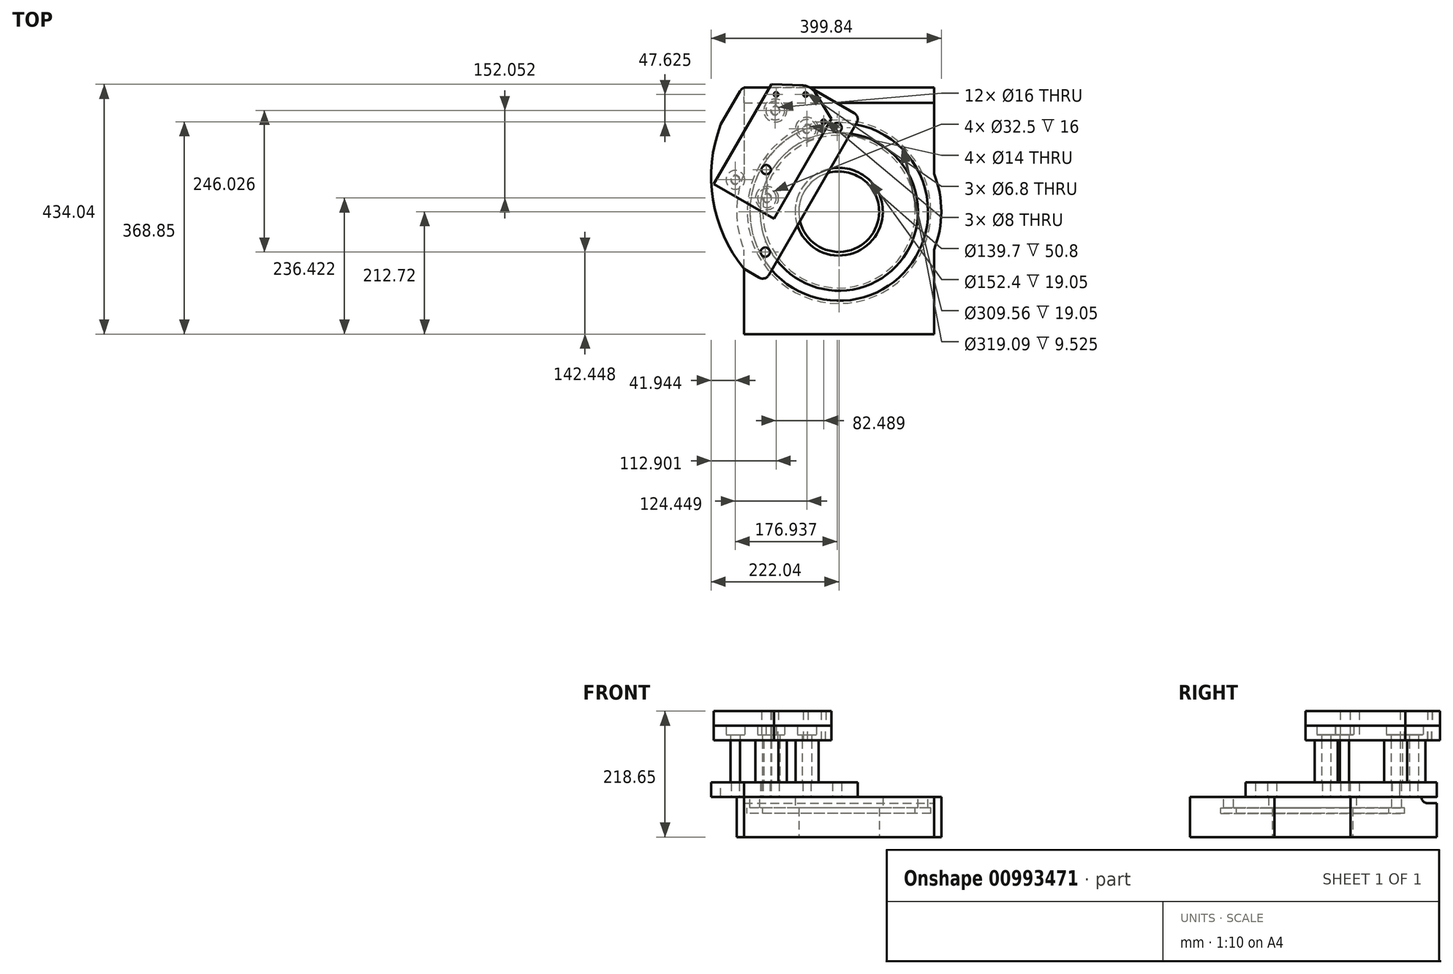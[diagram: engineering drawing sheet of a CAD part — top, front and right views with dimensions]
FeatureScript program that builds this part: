
annotation { "Feature Type Name" : "Feature", "Feature Type Description" : "" }
export const myFeature = defineFeature(function(context is Context, id is Id, definition is map)
    precondition{}
    {
        {
            var Q0;
            Q0=qCreatedBy(makeId("Top.planeOp"),FACE);
            var sketch = newSketch(context, id + "F0", { "sketchPlane" : qUnion([Q0])});
            skCircle(sketch, "E0", {"center": v(0, 0) * mm, "radius": 69.85 * mm});
            skCircle(sketch, "E1", {"center": v(0, 0) * mm, "radius": 76.2 * mm});
            skCircle(sketch, "E2", {"center": v(0, 0) * mm, "radius": 162.72 * mm});
            skCircle(sketch, "E3", {"center": v(0, 0) * mm, "radius": 137.32 * mm});
            skCircle(sketch, "E4", {"center": v(0, 0) * mm, "radius": 177.8 * mm});
            skLineSegment(sketch, "E5", {"start": v(0, 0) * mm, "end": v(0, 215.9) * mm, "construction": true});
            skLineSegment(sketch, "E6", {"start": v(0, 0) * mm, "end": v(0, -212.73) * mm, "construction": true});
            skLineSegment(sketch, "E7", {"start": v(0, 215.9) * mm, "end": v(-165.1, 215.9) * mm});
            skLineSegment(sketch, "E8", {"start": v(0, 215.9) * mm, "end": v(165.1, 215.9) * mm});
            skLineSegment(sketch, "E9", {"start": v(165.1, 215.9) * mm, "end": v(165.1, 66) * mm});
            skLineSegment(sketch, "E10", {"start": v(-165.1, 215.9) * mm, "end": v(-165.1, 66) * mm});
            skLineSegment(sketch, "E11", {"start": v(0, -212.72) * mm, "end": v(165.1, -212.72) * mm});
            skLineSegment(sketch, "E12", {"start": v(0, -212.73) * mm, "end": v(-165.1, -212.73) * mm});
            skLineSegment(sketch, "E13", {"start": v(165.1, -212.72) * mm, "end": v(165.1, -66) * mm});
            skLineSegment(sketch, "E14", {"start": v(-165.1, -212.73) * mm, "end": v(-165.1, -66) * mm});
            skSolve(sketch);
        }
        {
            var Q0;
            Q0=makeQuery(id+"F0.imprint","IMPRINT",FACE,{"disambiguationData":[TD([[makeQuery(id+"F0.imprint","IMPRINT",EDGE,{"derivedFrom":sQuery(id+"F0.wireOp",EDGE,"E11")}),1.0]])]});
            var Q1;
            Q1=makeQuery(id+"F0.imprint","IMPRINT",FACE,{"disambiguationData":[TD([[makeQuery(id+"F0.imprint","IMPRINT",EDGE,{"derivedFrom":sQuery(id+"F0.wireOp",EDGE,"E7")}),1.0]])]});
            var Q2;
            Q2=makeQuery(id+"F0.imprint","IMPRINT",FACE,{"disambiguationData":[TD([[makeQuery(id+"F0.imprint","IMPRINT",EDGE,{"derivedFrom":sQuery(id+"F0.wireOp",EDGE,"E2")}),-1.0]])]});
            var Q3;
            Q3=makeQuery(id+"F0.imprint","IMPRINT",FACE,{"disambiguationData":[TD([[makeQuery(id+"F0.imprint","IMPRINT",EDGE,{"derivedFrom":sQuery(id+"F0.wireOp",EDGE,"E2")}),1.0]])]});
            var Q4;
            Q4=makeQuery(id+"F0.imprint","IMPRINT",FACE,{"disambiguationData":[TD([[makeQuery(id+"F0.imprint","IMPRINT",EDGE,{"derivedFrom":sQuery(id+"F0.wireOp",EDGE,"E1")}),-1.0]])]});
            var Q5;
            Q5=makeQuery(id+"F0.imprint","IMPRINT",FACE,{"disambiguationData":[TD([[makeQuery(id+"F0.imprint","IMPRINT",EDGE,{"derivedFrom":sQuery(id+"F0.wireOp",EDGE,"E0")}),-1.0]])]});
            extrude(context, id + "F1", {"entities" : qUnion([Q0, Q1, Q2, Q3, Q4, Q5]), "depth" : 69.85 * mm, "offsetDistance" : 25.4 * mm});
        }
        {
            var Q0;
            Q0=makeQuery(id+"F0.imprint","IMPRINT",FACE,{"disambiguationData":[TD([[makeQuery(id+"F0.imprint","IMPRINT",EDGE,{"derivedFrom":sQuery(id+"F0.wireOp",EDGE,"E0")}),-1.0]])]});
            var Q1;
            Q1=makeQuery(id+"F1.opExtrude","CAP_FACE",FACE,{"disambiguationData":[OSD([sQuery(id+"F0.wireOp",EDGE,"E0"),sQuery(id+"F0.wireOp",EDGE,"E4"),sQuery(id+"F0.wireOp",EDGE,"E7"),sQuery(id+"F0.wireOp",EDGE,"E8"),sQuery(id+"F0.wireOp",EDGE,"E9"),sQuery(id+"F0.wireOp",EDGE,"E10"),sQuery(id+"F0.wireOp",EDGE,"E11"),sQuery(id+"F0.wireOp",EDGE,"E12"),sQuery(id+"F0.wireOp",EDGE,"E13"),sQuery(id+"F0.wireOp",EDGE,"E14")])],"isStart":false});
            var Q2;
            Q2=makeQuery(id+"F1.opExtrude","CAP_FACE",FACE,{"disambiguationData":[OSD([sQuery(id+"F0.wireOp",EDGE,"E0"),sQuery(id+"F0.wireOp",EDGE,"E4"),sQuery(id+"F0.wireOp",EDGE,"E7"),sQuery(id+"F0.wireOp",EDGE,"E8"),sQuery(id+"F0.wireOp",EDGE,"E9"),sQuery(id+"F0.wireOp",EDGE,"E10"),sQuery(id+"F0.wireOp",EDGE,"E11"),sQuery(id+"F0.wireOp",EDGE,"E12"),sQuery(id+"F0.wireOp",EDGE,"E13"),sQuery(id+"F0.wireOp",EDGE,"E14")])],"isStart":false});
            extrude(context, id + "F2", {"entities" : qUnion([Q0]), "operationType" : NewBodyOperationType.REMOVE, "endBound" : BoundingType.UP_TO_SURFACE, "depth" : 19.05 * mm, "endBoundEntityFace" : qUnion([Q1]), "offsetDistance" : 25.4 * mm, "hasSecondDirection" : true, "secondDirectionBound" : BoundingType.UP_TO_SURFACE, "secondDirectionOppositeDirection" : false, "secondDirectionDepth" : 25.4 * mm, "secondDirectionBoundEntityFace" : qUnion([Q2]), "hasSecondDirectionOffset" : true, "secondDirectionOffsetDistance" : 19.05 * mm});
        }
        {
            var Q0;
            Q0=qCreatedBy(makeId("Right.planeOp"),FACE);
            var sketch = newSketch(context, id + "F3", { "sketchPlane" : qUnion([Q0])});
            skLineSegment(sketch, "E15.0", {"start": v(215.9, 69.85) * mm, "end": v(66, 69.85) * mm});
            skLineSegment(sketch, "E16.0", {"start": v(66, 69.85) * mm, "end": v(-66, 69.85) * mm});
            skLineSegment(sketch, "E17.0", {"start": v(-212.73, 69.85) * mm, "end": v(-66, 69.85) * mm});
            skLineSegment(sketch, "E18.0", {"start": v(215.9, 69.85) * mm, "end": v(215.9, 0) * mm});
            skLineSegment(sketch, "E19.0", {"start": v(-212.73, 69.85) * mm, "end": v(-212.73, 0) * mm});
            skLineSegment(sketch, "E20.0", {"start": v(-212.73, 0) * mm, "end": v(-66, 0) * mm});
            skLineSegment(sketch, "E21.0", {"start": v(-162.72, 0) * mm, "end": v(162.72, 0) * mm});
            skLineSegment(sketch, "E22.0", {"start": v(215.9, 0) * mm, "end": v(66, 0) * mm});
            skLineSegment(sketch, "E23", {"start": v(215.9, 58.74) * mm, "end": v(188.91, 58.74) * mm});
            skLineSegment(sketch, "E24", {"start": v(188.91, 58.74) * mm, "end": v(188.91, 69.85) * mm, "construction": true});
            skPoint(sketch, "E25", {"position": v(200.02, 69.85) * mm});
            skArc(sketch, "E26", {"start": v(188.91, 69.85) * mm, "mid": v(192.17, 62) * mm, "end": v(200.02, 58.74) * mm});
            skLineSegment(sketch, "E27", {"start": v(0, 0) * mm, "end": v(0, 69.85) * mm, "construction": true});
            skPoint(sketch, "E28", {"position": v(137.32, 69.85) * mm});
            skPoint(sketch, "E29", {"position": v(154.78, 69.85) * mm});
            skLineSegment(sketch, "E30", {"start": v(154.78, 69.85) * mm, "end": v(154.78, 50.8) * mm});
            skLineSegment(sketch, "E31", {"start": v(137.32, 69.85) * mm, "end": v(137.32, 50.8) * mm});
            skLineSegment(sketch, "E32", {"start": v(154.78, 50.8) * mm, "end": v(159.54, 50.8) * mm});
            skLineSegment(sketch, "E33", {"start": v(137.32, 50.8) * mm, "end": v(132.56, 50.8) * mm});
            skLineSegment(sketch, "E34", {"start": v(159.54, 50.8) * mm, "end": v(159.54, 41.28) * mm});
            skLineSegment(sketch, "E35", {"start": v(159.54, 41.28) * mm, "end": v(132.56, 41.28) * mm});
            skLineSegment(sketch, "E36", {"start": v(132.56, 41.28) * mm, "end": v(132.56, 50.8) * mm});
            skSolve(sketch);
        }
        {
            var Q0;
            {var subQ3=sQuery(id+"F3.wireOp",EDGE,"E26");Q0=makeQuery(id+"F3.imprint","IMPRINT",FACE,{"disambiguationData":[TD([[makeQuery(id+"F3.imprint","IMPRINT",EDGE,{"derivedFrom":subQ3}),1.0]])]});}
            extrude(context, id + "F4", {"entities" : qUnion([Q0]), "operationType" : NewBodyOperationType.REMOVE, "endBound" : BoundingType.THROUGH_ALL, "oppositeDirection" : true, "depth" : 25.4 * mm, "offsetDistance" : 25.4 * mm, "hasSecondDirection" : true, "secondDirectionBound" : BoundingType.THROUGH_ALL, "secondDirectionOppositeDirection" : false, "secondDirectionDepth" : 25.4 * mm});
        }
        {
            var Q0;
            {var subQ1=sQuery(id+"F3.wireOp",EDGE,"E30");Q0=makeQuery(id+"F3.imprint","IMPRINT",FACE,{"disambiguationData":[TD([[makeQuery(id+"F3.imprint","IMPRINT",EDGE,{"derivedFrom":subQ1}),-1.0]])]});}
            var Q1;
            Q1=sQuery(id+"F3.wireOp",EDGE,"E27");
            revolve(context, id + "F5", {"operationType" : NewBodyOperationType.REMOVE, "surfaceOperationType" : NewSurfaceOperationType.NEW, "entities" : qUnion([Q0]), "axis" : qUnion([Q1]), "revolveType" : RevolveType.FULL, "oppositeDirection" : true});
        }
        {
            var Q0;
            {var subQ0=sQuery(id+"F0.wireOp",EDGE,"E10");var subQ1=sQuery(id+"F0.wireOp",EDGE,"E9");var subQ2=sQuery(id+"F0.wireOp",EDGE,"E4");var subQ3=sQuery(id+"F0.wireOp",EDGE,"E13");var subQ4=sQuery(id+"F0.wireOp",EDGE,"E14");var subQ5=sQuery(id+"F0.wireOp",EDGE,"E12");var subQ6=sQuery(id+"F0.wireOp",EDGE,"E11");Q0=makeQuery(id+"F5.boolean.opBoolean","SPLIT",FACE,{"disambiguationData":[TD([makeQuery(id+"F1.opExtrude","SWEPT_FACE",FACE,{"disambiguationData":[OSD([subQ1])]})])],"derivedFrom":makeQuery(id+"F1.opExtrude","CAP_FACE",FACE,{"disambiguationData":[OSD([sQuery(id+"F0.wireOp",EDGE,"E0"),subQ2,sQuery(id+"F0.wireOp",EDGE,"E7"),sQuery(id+"F0.wireOp",EDGE,"E8"),subQ1,subQ0,subQ6,subQ5,subQ3,subQ4])],"isStart":false})});}
            cPlane(context, id + "F6", {"entities" : qUnion([Q0]), "cplaneType" : CPlaneType.OFFSET, "offset" : 225 * mm, "width" : 152.4 * mm, "height" : 152.4 * mm});
        }
        {
            var Q0;
            {var subQ0=sQuery(id+"F0.wireOp",EDGE,"E10");var subQ1=sQuery(id+"F0.wireOp",EDGE,"E9");var subQ2=sQuery(id+"F0.wireOp",EDGE,"E4");var subQ3=sQuery(id+"F0.wireOp",EDGE,"E13");var subQ4=sQuery(id+"F0.wireOp",EDGE,"E14");var subQ5=sQuery(id+"F0.wireOp",EDGE,"E12");var subQ6=sQuery(id+"F0.wireOp",EDGE,"E11");Q0=makeQuery(id+"F5.boolean.opBoolean","SPLIT",FACE,{"disambiguationData":[TD([makeQuery(id+"F1.opExtrude","SWEPT_FACE",FACE,{"disambiguationData":[OSD([subQ1])]})])],"derivedFrom":makeQuery(id+"F1.opExtrude","CAP_FACE",FACE,{"disambiguationData":[OSD([sQuery(id+"F0.wireOp",EDGE,"E0"),subQ2,sQuery(id+"F0.wireOp",EDGE,"E7"),sQuery(id+"F0.wireOp",EDGE,"E8"),subQ1,subQ0,subQ6,subQ5,subQ3,subQ4])],"isStart":false})});}
            var sketch = newSketch(context, id + "F7", { "sketchPlane" : qUnion([Q0])});
            skLineSegment(sketch, "E37.0", {"start": v(-165.1, 215.9) * mm, "end": v(165.1, 215.9) * mm});
            skPoint(sketch, "E38", {"position": v(-50.8, 215.9) * mm});
            skLineSegment(sketch, "E39", {"start": v(-50.8, 215.9) * mm, "end": v(-127.79, 260.35) * mm});
            skLineSegment(sketch, "E40", {"start": v(-50.8, 215.9) * mm, "end": v(26.19, 171.45) * mm});
            skLineSegment(sketch, "E41", {"start": v(30.84, 154.1) * mm, "end": v(-121.56, -109.86) * mm});
            skLineSegment(sketch, "E42", {"start": v(-145.14, 255.7) * mm, "end": v(-303.89, -19.26) * mm});
            skLineSegment(sketch, "E43", {"start": v(-138.91, -114.51) * mm, "end": v(-303.89, -19.26) * mm});
            skPoint(sketch, "E44", {"position": v(-253.09, 68.73) * mm});
            skLineSegment(sketch, "E45.0", {"start": v(-165.1, -212.73) * mm, "end": v(-165.1, -66) * mm});
            skPoint(sketch, "E46", {"position": v(-165.1, -99.4) * mm});
            skCircle(sketch, "E47.0", {"center": v(0, 0) * mm, "radius": 154.78 * mm});
            skCircle(sketch, "E48.0", {"center": v(0, 0) * mm, "radius": 137.32 * mm});
            skCircle(sketch, "E49.0", {"center": v(0, 0) * mm, "radius": 146.05 * mm, "construction": true});
            skLineSegment(sketch, "E50.0", {"start": v(-3.16, 146.02) * mm, "end": v(-128.03, -70.27) * mm, "construction": true});
            skPoint(sketch, "E51", {"position": v(-3.16, 146.02) * mm});
            skPoint(sketch, "E52", {"position": v(-128.03, -70.27) * mm});
            skLineSegment(sketch, "E53", {"start": v(-65.6, 37.87) * mm, "end": v(-126.48, 73.02) * mm, "construction": true});
            skPoint(sketch, "E54", {"position": v(-126.48, 73.02) * mm});
            skArc(sketch, "E55", {"start": v(-253.09, 68.73) * mm, "mid": v(-229.92, -26.23) * mm, "end": v(-165.1, -99.4) * mm});
            skPoint(sketch, "E56.visualSharp", {"position": v(-138.79, 266.7) * mm});
            skArc(sketch, "E56.filletArc", {"start": v(-127.79, 260.35) * mm, "mid": v(-137.43, 261.62) * mm, "end": v(-145.14, 255.7) * mm});
            skPoint(sketch, "E57.visualSharp", {"position": v(37.19, 165.1) * mm});
            skArc(sketch, "E57.filletArc", {"start": v(30.84, 154.1) * mm, "mid": v(32.1, 163.74) * mm, "end": v(26.19, 171.45) * mm});
            skPoint(sketch, "E58.visualSharp", {"position": v(-127.91, -120.86) * mm});
            skArc(sketch, "E58.filletArc", {"start": v(-138.91, -114.51) * mm, "mid": v(-129.27, -115.78) * mm, "end": v(-121.56, -109.86) * mm});
            skSolve(sketch);
        }
        {
            var Q0;
            {var subQ7=sQuery(id+"F7.wireOp",EDGE,"E39");Q0=makeQuery(id+"F7.imprint","IMPRINT",FACE,{"disambiguationData":[TD([[makeQuery(id+"F7.imprint","IMPRINT",EDGE,{"derivedFrom":subQ7}),1.0]])]});}
            var Q1;
            {var subQ12=sQuery(id+"F0.wireOp",EDGE,"E10");var subQ15=makeQuery(id+"F1.opExtrude","CAP_EDGE",EDGE,{"disambiguationData":[OSD([subQ12])],"isStart":false});Q1=makeQuery(id+"F7.imprint","IMPRINT",FACE,{"disambiguationData":[TD([[makeQuery(id+"F7.imprint","IMPRINT",EDGE,{"derivedFrom":subQ15}),1.0]])]});}
            var Q2;
            {var subQ0=sQuery(id+"F7.wireOp",EDGE,"E48.0");var subQ1=sQuery(id+"F7.wireOp",EDGE,"E41");var subQ2=makeQuery(id+"F7.imprint","INTERSECT",VERTEX,{"disambiguationData":[OD(0.0)],"derivedFrom":[subQ1,subQ0]});Q2=makeQuery(id+"F7.imprint","IMPRINT",FACE,{"disambiguationData":[TD([[makeQuery(id+"F7.imprint","IMPRINT",EDGE,{"disambiguationData":[TD([[subQ2,-1.0]])],"derivedFrom":subQ1}),-1.0]])]});}
            var Q3;
            {var subQ0=sQuery(id+"F7.wireOp",EDGE,"E47.0");var subQ1=sQuery(id+"F7.wireOp",EDGE,"E41");var subQ2=makeQuery(id+"F7.imprint","INTERSECT",VERTEX,{"disambiguationData":[OD(0.0)],"derivedFrom":[subQ1,subQ0]});Q3=makeQuery(id+"F7.imprint","IMPRINT",FACE,{"disambiguationData":[TD([[makeQuery(id+"F7.imprint","IMPRINT",EDGE,{"disambiguationData":[TD([[subQ2,-1.0]])],"derivedFrom":subQ1}),-1.0]])]});}
            var Q4;
            {var subQ3=sQuery(id+"F7.wireOp",EDGE,"ZGJADGpM-cLlG-fw4n-4Hqn-Gagi5i82YWmQ");Q4=makeQuery(id+"F7.imprint","IMPRINT",FACE,{"disambiguationData":[TD([[makeQuery(id+"F7.imprint","IMPRINT",EDGE,{"derivedFrom":subQ3}),-1.0]])]});}
            extrude(context, id + "F8", {"entities" : qUnion([Q0, Q1, Q2, Q3, Q4]), "depth" : 25 * mm, "offsetDistance" : 25.4 * mm});
        }
        {
            var Q0;
            Q0=makeQuery(id+"F8.opExtrude","CAP_FACE",FACE,{"disambiguationData":[OSD([sQuery(id+"F7.wireOp",EDGE,"E39"),sQuery(id+"F7.wireOp",EDGE,"E40"),sQuery(id+"F7.wireOp",EDGE,"E41"),sQuery(id+"F7.wireOp",EDGE,"E42"),sQuery(id+"F7.wireOp",EDGE,"E43")])],"isStart":false});
            var sketch = newSketch(context, id + "F9", { "sketchPlane" : qUnion([Q0])});
            skPoint(sketch, "E59.0", {"position": v(-3.16, 146.02) * mm});
            skPoint(sketch, "E60.0", {"position": v(-126.48, 73.02) * mm});
            skPoint(sketch, "E61.0", {"position": v(-128.03, -70.27) * mm});
            skSolve(sketch);
        }
        {
            var Q0;
            Q0=sQuery(id+"F9.wireOp",VERTEX,"E59.0");
            var Q1;
            Q1=sQuery(id+"F9.wireOp",VERTEX,"E60.0");
            var Q2;
            Q2=sQuery(id+"F9.wireOp",VERTEX,"E61.0");
            var Q3;
            Q3=makeQuery(id+"F8.opExtrude","SWEPT_BODY",BODY,{"disambiguationData":[OSD([sQuery(id+"F7.wireOp",EDGE,"E39"),sQuery(id+"F7.wireOp",EDGE,"E40"),sQuery(id+"F7.wireOp",EDGE,"E41"),sQuery(id+"F7.wireOp",EDGE,"E42"),sQuery(id+"F7.wireOp",EDGE,"E43")])]});
            hole(context, id + "F10", {"style" : HoleStyle.SIMPLE, "endStyle" : HoleEndStyle.THROUGH, "holeDiameter" : 16 * mm, "majorDiameter" : 6.35 * mm, "isTappedThrough" : true, "tappedDepth" : 12.7 * mm, "tapClearance" : 3, "startFromSketch" : true, "locations" : qUnion([Q0, Q1, Q2]), "scope" : qUnion([Q3])});
        }
        {
            var Q0;
            Q0=qCreatedBy(id+"F6.planeOp",FACE);
            cPlane(context, id + "F11", {"entities" : qUnion([Q0]), "cplaneType" : CPlaneType.OFFSET, "offset" : 101.6 * mm, "oppositeDirection" : true, "width" : 152.4 * mm, "height" : 152.4 * mm});
        }
        {
            var Q0;
            Q0=makeQuery(id+"F8.opExtrude","CAP_FACE",FACE,{"disambiguationData":[OSD([sQuery(id+"F7.wireOp",EDGE,"E39"),sQuery(id+"F7.wireOp",EDGE,"E40"),sQuery(id+"F7.wireOp",EDGE,"E41"),sQuery(id+"F7.wireOp",EDGE,"E42"),sQuery(id+"F7.wireOp",EDGE,"E43"),sQuery(id+"F7.wireOp",EDGE,"E55"),sQuery(id+"F7.wireOp",EDGE,"E56.filletArc"),sQuery(id+"F7.wireOp",EDGE,"E57.filletArc"),sQuery(id+"F7.wireOp",EDGE,"E58.filletArc")])],"isStart":false});
            var sketch = newSketch(context, id + "F12", { "sketchPlane" : qUnion([Q0])});
            skArc(sketch, "E62.0.0", {"start": v(-253.09, 68.73) * mm, "mid": v(-229.92, -26.23) * mm, "end": v(-165.1, -99.4) * mm});
            skLineSegment(sketch, "E62.0.1", {"start": v(-165.1, -99.4) * mm, "end": v(-138.91, -114.51) * mm});
            skArc(sketch, "E62.0.2", {"start": v(-138.91, -114.51) * mm, "mid": v(-129.27, -115.78) * mm, "end": v(-121.56, -109.86) * mm});
            skLineSegment(sketch, "E62.0.3", {"start": v(-121.56, -109.86) * mm, "end": v(30.84, 154.1) * mm});
            skArc(sketch, "E62.0.4", {"start": v(30.84, 154.1) * mm, "mid": v(32.1, 163.74) * mm, "end": v(26.19, 171.45) * mm});
            skLineSegment(sketch, "E62.0.5", {"start": v(26.19, 171.45) * mm, "end": v(-127.79, 260.35) * mm});
            skArc(sketch, "E62.0.6", {"start": v(-127.79, 260.35) * mm, "mid": v(-137.43, 261.62) * mm, "end": v(-145.14, 255.7) * mm});
            skLineSegment(sketch, "E62.0.7", {"start": v(-145.14, 255.7) * mm, "end": v(-253.09, 68.73) * mm});
            skLineSegment(sketch, "E63", {"start": v(-50.8, 215.9) * mm, "end": v(-57.94, 203.53) * mm, "construction": true});
            skLineSegment(sketch, "E64", {"start": v(-57.94, 203.53) * mm, "end": v(-70.64, 181.53) * mm, "construction": true});
            skLineSegment(sketch, "E65", {"start": v(-70.64, 181.53) * mm, "end": v(-26.65, 156.13) * mm, "construction": true});
            skLineSegment(sketch, "E66", {"start": v(-70.64, 181.53) * mm, "end": v(-109.14, 203.75) * mm, "construction": true});
            skLineSegment(sketch, "E67", {"start": v(-70.64, 181.53) * mm, "end": v(-165.1, 17.93) * mm, "construction": true});
            skLineSegment(sketch, "E68", {"start": v(-165.1, 17.93) * mm, "end": v(-112.86, -12.24) * mm});
            skLineSegment(sketch, "E69", {"start": v(-165.1, 17.93) * mm, "end": v(-217.34, 48.09) * mm});
            skLineSegment(sketch, "E70", {"start": v(-112.86, -12.24) * mm, "end": v(-12.84, 161) * mm});
            skLineSegment(sketch, "E71", {"start": v(-217.34, 48.09) * mm, "end": v(-117.33, 221.32) * mm});
            skPoint(sketch, "E72.visualSharp", {"position": v(-50.8, 215.9) * mm});
            skPoint(sketch, "E73", {"position": v(-57.94, 203.53) * mm});
            skPoint(sketch, "E74", {"position": v(-26.65, 156.13) * mm});
            skPoint(sketch, "E75", {"position": v(-109.14, 203.75) * mm});
            skPoint(sketch, "E76", {"position": v(-63.5, 193.9) * mm});
            skArc(sketch, "E77", {"start": v(-41.99, 207.4) * mm, "mid": v(-50.8, 215.9) * mm, "end": v(-62.56, 219.29) * mm});
            skLineSegment(sketch, "E78", {"start": v(-12.84, 161) * mm, "end": v(-41.99, 207.4) * mm});
            skLineSegment(sketch, "E79.MirrorCS", {"start": v(-117.33, 221.32) * mm, "end": v(-62.56, 219.29) * mm});
            skCircle(sketch, "E80", {"center": v(-57.94, 203.53) * mm, "radius": 4 * mm});
            skCircle(sketch, "E81", {"center": v(-26.65, 156.13) * mm, "radius": 4 * mm});
            skCircle(sketch, "E82", {"center": v(-109.14, 203.75) * mm, "radius": 4 * mm});
            skPoint(sketch, "E83", {"position": v(-152.6, 39.58) * mm});
            skPoint(sketch, "E84", {"position": v(-83.14, 159.88) * mm});
            skLineSegment(sketch, "E85", {"start": v(-83.14, 159.88) * mm, "end": v(-55.65, 144) * mm, "construction": true});
            skLineSegment(sketch, "E86", {"start": v(-83.14, 159.88) * mm, "end": v(-110.64, 175.75) * mm, "construction": true});
            skCircle(sketch, "E87", {"center": v(-55.65, 144) * mm, "radius": 20 * mm});
            skCircle(sketch, "E88", {"center": v(-55.65, 144) * mm, "radius": 8 * mm});
            skCircle(sketch, "E89", {"center": v(-110.64, 175.75) * mm, "radius": 20 * mm});
            skCircle(sketch, "E90", {"center": v(-110.64, 175.75) * mm, "radius": 8 * mm});
            skLineSegment(sketch, "E91", {"start": v(-152.6, 39.58) * mm, "end": v(-125.1, 23.7) * mm, "construction": true});
            skLineSegment(sketch, "E92", {"start": v(-152.6, 39.58) * mm, "end": v(-180.1, 55.45) * mm, "construction": true});
            skCircle(sketch, "E93", {"center": v(-125.1, 23.7) * mm, "radius": 8 * mm});
            skCircle(sketch, "E94", {"center": v(-125.1, 23.7) * mm, "radius": 20 * mm});
            skCircle(sketch, "E95.MirrorC", {"center": v(-180.1, 55.45) * mm, "radius": 8 * mm});
            skCircle(sketch, "E96.MirrorC", {"center": v(-180.1, 55.45) * mm, "radius": 20 * mm});
            skSolve(sketch);
        }
        {
            var Q0;
            Q0=makeQuery(id+"F12.imprint","IMPRINT",FACE,{"disambiguationData":[TD([[makeQuery(id+"F12.imprint","IMPRINT",EDGE,{"derivedFrom":sQuery(id+"F12.wireOp",EDGE,"E68")}),1.0]])]});
            var Q1;
            Q1=makeQuery(id+"F12.imprint","IMPRINT",FACE,{"disambiguationData":[TD([[makeQuery(id+"F12.imprint","IMPRINT",EDGE,{"derivedFrom":makeQuery(id+"F10.hole-1.boolean.opBoolean","COPY",EDGE,{"derivedFrom":makeQuery(id+"F10.hole-1.opRevolve","SWEPT_EDGE",EDGE,{"disambiguationData":[OSD([sQuery(id+"F10.hole-1.sketch.wireOp",EDGE,"core_line_2"),sQuery(id+"F10.hole-1.sketch.wireOp",EDGE,"core_line_3")])]})})}),1.0]])]});
            var Q2;
            Q2=makeQuery(id+"F12.imprint","IMPRINT",FACE,{"disambiguationData":[TD([[makeQuery(id+"F12.imprint","IMPRINT",EDGE,{"derivedFrom":sQuery(id+"F12.wireOp",EDGE,"E89")}),1.0]])]});
            var Q3;
            Q3=makeQuery(id+"F12.imprint","IMPRINT",FACE,{"disambiguationData":[TD([[makeQuery(id+"F12.imprint","IMPRINT",EDGE,{"derivedFrom":sQuery(id+"F12.wireOp",EDGE,"E87")}),1.0]])]});
            var Q4;
            Q4=makeQuery(id+"F12.imprint","IMPRINT",FACE,{"disambiguationData":[TD([[makeQuery(id+"F12.imprint","IMPRINT",EDGE,{"derivedFrom":sQuery(id+"F12.wireOp",EDGE,"E93")}),-1.0]])]});
            var Q5;
            Q5=makeQuery(id+"F12.imprint","IMPRINT",FACE,{"disambiguationData":[TD([[makeQuery(id+"F12.imprint","IMPRINT",EDGE,{"derivedFrom":sQuery(id+"F12.wireOp",EDGE,"E95.MirrorC")}),1.0]])]});
            var Q6;
            Q6=makeQuery(id+"F12.imprint","IMPRINT",FACE,{"disambiguationData":[TD([[makeQuery(id+"F12.imprint","IMPRINT",EDGE,{"derivedFrom":sQuery(id+"F12.wireOp",EDGE,"E90")}),1.0]])]});
            var Q7;
            Q7=makeQuery(id+"F12.imprint","IMPRINT",FACE,{"disambiguationData":[TD([[makeQuery(id+"F12.imprint","IMPRINT",EDGE,{"derivedFrom":sQuery(id+"F12.wireOp",EDGE,"E88")}),1.0]])]});
            var Q8;
            Q8=makeQuery(id+"F12.imprint","IMPRINT",FACE,{"disambiguationData":[TD([[makeQuery(id+"F12.imprint","IMPRINT",EDGE,{"derivedFrom":sQuery(id+"F12.wireOp",EDGE,"E93")}),1.0]])]});
            var Q9;
            Q9=makeQuery(id+"F12.imprint","IMPRINT",FACE,{"disambiguationData":[TD([[makeQuery(id+"F12.imprint","IMPRINT",EDGE,{"derivedFrom":sQuery(id+"F12.wireOp",EDGE,"E95.MirrorC")}),-1.0]])]});
            var Q10;
            Q10=qCreatedBy(id+"F11.planeOp",FACE);
            var Q11;
            Q11=qCreatedBy(id+"F11.planeOp",FACE);
            extrude(context, id + "F13", {"entities" : qUnion([Q0, Q1, Q2, Q3, Q4, Q5, Q6, Q7, Q8, Q9]), "endBound" : BoundingType.UP_TO_SURFACE, "depth" : 25.4 * mm, "endBoundEntityFace" : qUnion([Q10]), "hasOffset" : true, "offsetDistance" : 25.4 * mm, "offsetOppositeDirection" : true, "hasSecondDirection" : true, "secondDirectionBound" : BoundingType.UP_TO_SURFACE, "secondDirectionOppositeDirection" : false, "secondDirectionDepth" : 25.4 * mm, "secondDirectionBoundEntityFace" : qUnion([Q11])});
        }
        {
            var Q0;
            Q0=makeQuery(id+"F12.imprint","IMPRINT",FACE,{"disambiguationData":[TD([[makeQuery(id+"F12.imprint","IMPRINT",EDGE,{"derivedFrom":sQuery(id+"F12.wireOp",EDGE,"E68")}),1.0]])]});
            var Q1;
            Q1=makeQuery(id+"F12.imprint","IMPRINT",FACE,{"disambiguationData":[TD([[makeQuery(id+"F12.imprint","IMPRINT",EDGE,{"derivedFrom":sQuery(id+"F12.wireOp",EDGE,"E87")}),1.0]])]});
            var Q2;
            Q2=makeQuery(id+"F12.imprint","IMPRINT",FACE,{"disambiguationData":[TD([[makeQuery(id+"F12.imprint","IMPRINT",EDGE,{"derivedFrom":sQuery(id+"F12.wireOp",EDGE,"E89")}),1.0]])]});
            var Q3;
            Q3=makeQuery(id+"F12.imprint","IMPRINT",FACE,{"disambiguationData":[TD([[makeQuery(id+"F12.imprint","IMPRINT",EDGE,{"derivedFrom":sQuery(id+"F12.wireOp",EDGE,"E95.MirrorC")}),1.0]])]});
            var Q4;
            Q4=makeQuery(id+"F12.imprint","IMPRINT",FACE,{"disambiguationData":[TD([[makeQuery(id+"F12.imprint","IMPRINT",EDGE,{"derivedFrom":sQuery(id+"F12.wireOp",EDGE,"E93")}),-1.0]])]});
            var Q5;
            Q5=makeQuery(id+"F12.imprint","IMPRINT",FACE,{"disambiguationData":[TD([[makeQuery(id+"F12.imprint","IMPRINT",EDGE,{"derivedFrom":makeQuery(id+"F10.hole-1.boolean.opBoolean","COPY",EDGE,{"derivedFrom":makeQuery(id+"F10.hole-1.opRevolve","SWEPT_EDGE",EDGE,{"disambiguationData":[OSD([sQuery(id+"F10.hole-1.sketch.wireOp",EDGE,"core_line_2"),sQuery(id+"F10.hole-1.sketch.wireOp",EDGE,"core_line_3")])]})})}),1.0]])]});
            var Q6;
            Q6=makeQuery(id+"F12.imprint","IMPRINT",FACE,{"disambiguationData":[TD([[makeQuery(id+"F12.imprint","IMPRINT",EDGE,{"derivedFrom":sQuery(id+"F12.wireOp",EDGE,"E90")}),1.0]])]});
            var Q7;
            Q7=makeQuery(id+"F12.imprint","IMPRINT",FACE,{"disambiguationData":[TD([[makeQuery(id+"F12.imprint","IMPRINT",EDGE,{"derivedFrom":sQuery(id+"F12.wireOp",EDGE,"E88")}),1.0]])]});
            var Q8;
            Q8=makeQuery(id+"F12.imprint","IMPRINT",FACE,{"disambiguationData":[TD([[makeQuery(id+"F12.imprint","IMPRINT",EDGE,{"derivedFrom":sQuery(id+"F12.wireOp",EDGE,"E95.MirrorC")}),-1.0]])]});
            var Q9;
            Q9=makeQuery(id+"F12.imprint","IMPRINT",FACE,{"disambiguationData":[TD([[makeQuery(id+"F12.imprint","IMPRINT",EDGE,{"derivedFrom":sQuery(id+"F12.wireOp",EDGE,"E93")}),1.0]])]});
            var Q10;
            Q10=makeQuery(id+"F12.imprint","IMPRINT",FACE,{"disambiguationData":[TD([[makeQuery(id+"F12.imprint","IMPRINT",EDGE,{"derivedFrom":sQuery(id+"F12.wireOp",EDGE,"E80")}),1.0]])]});
            var Q11;
            Q11=makeQuery(id+"F12.imprint","IMPRINT",FACE,{"disambiguationData":[TD([[makeQuery(id+"F12.imprint","IMPRINT",EDGE,{"derivedFrom":sQuery(id+"F12.wireOp",EDGE,"E82")}),1.0]])]});
            var Q12;
            Q12=makeQuery(id+"F12.imprint","IMPRINT",FACE,{"disambiguationData":[TD([[makeQuery(id+"F12.imprint","IMPRINT",EDGE,{"derivedFrom":sQuery(id+"F12.wireOp",EDGE,"E81")}),1.0]])]});
            var Q13;
            Q13=qCreatedBy(id+"F11.planeOp",FACE);
            var Q14;
            Q14=qCreatedBy(id+"F11.planeOp",FACE);
            extrude(context, id + "F14", {"entities" : qUnion([Q0, Q1, Q2, Q3, Q4, Q5, Q6, Q7, Q8, Q9, Q10, Q11, Q12]), "endBound" : BoundingType.UP_TO_SURFACE, "depth" : 25.4 * mm, "endBoundEntityFace" : qUnion([Q13]), "offsetDistance" : 25.4 * mm, "hasSecondDirection" : true, "secondDirectionBound" : BoundingType.UP_TO_SURFACE, "secondDirectionOppositeDirection" : false, "secondDirectionDepth" : 25.4 * mm, "secondDirectionBoundEntityFace" : qUnion([Q14]), "hasSecondDirectionOffset" : true, "secondDirectionOffsetDistance" : 25 * mm});
        }
        {
            var Q0;
            Q0=makeQuery(id+"F12.imprint","IMPRINT",FACE,{"disambiguationData":[TD([[makeQuery(id+"F12.imprint","IMPRINT",EDGE,{"derivedFrom":sQuery(id+"F12.wireOp",EDGE,"E87")}),1.0]])]});
            var Q1;
            Q1=makeQuery(id+"F12.imprint","IMPRINT",FACE,{"disambiguationData":[TD([[makeQuery(id+"F12.imprint","IMPRINT",EDGE,{"derivedFrom":sQuery(id+"F12.wireOp",EDGE,"E89")}),1.0]])]});
            var Q2;
            Q2=makeQuery(id+"F12.imprint","IMPRINT",FACE,{"disambiguationData":[TD([[makeQuery(id+"F12.imprint","IMPRINT",EDGE,{"derivedFrom":sQuery(id+"F12.wireOp",EDGE,"E95.MirrorC")}),1.0]])]});
            var Q3;
            Q3=makeQuery(id+"F12.imprint","IMPRINT",FACE,{"disambiguationData":[TD([[makeQuery(id+"F12.imprint","IMPRINT",EDGE,{"derivedFrom":sQuery(id+"F12.wireOp",EDGE,"E93")}),-1.0]])]});
            var Q4;
            Q4=makeQuery(id+"F14.opExtrude","CAP_FACE",FACE,{"disambiguationData":[OSD([sQuery(id+"F12.wireOp",EDGE,"E68"),sQuery(id+"F12.wireOp",EDGE,"E69"),sQuery(id+"F12.wireOp",EDGE,"E70"),sQuery(id+"F12.wireOp",EDGE,"E71"),sQuery(id+"F12.wireOp",EDGE,"E77"),sQuery(id+"F12.wireOp",EDGE,"E78"),sQuery(id+"F12.wireOp",EDGE,"E79.MirrorCS"),sQuery(id+"F12.wireOp",EDGE,"E80"),sQuery(id+"F12.wireOp",EDGE,"E81"),sQuery(id+"F12.wireOp",EDGE,"E82"),sQuery(id+"F12.wireOp",EDGE,"E88"),sQuery(id+"F12.wireOp",EDGE,"E90"),sQuery(id+"F12.wireOp",EDGE,"E93"),sQuery(id+"F12.wireOp",EDGE,"E95.MirrorC")])],"isStart":true});
            extrude(context, id + "F15", {"entities" : qUnion([Q0, Q1, Q2, Q3]), "endBound" : BoundingType.UP_TO_SURFACE, "depth" : 25.4 * mm, "endBoundEntityFace" : qUnion([Q4]), "offsetDistance" : 25.4 * mm});
        }
        {
            var Q0;
            Q0=makeQuery(id+"F14.opExtrude","CAP_FACE",FACE,{"disambiguationData":[OSD([sQuery(id+"F12.wireOp",EDGE,"E68"),sQuery(id+"F12.wireOp",EDGE,"E69"),sQuery(id+"F12.wireOp",EDGE,"E70"),sQuery(id+"F12.wireOp",EDGE,"E71"),sQuery(id+"F12.wireOp",EDGE,"E77"),sQuery(id+"F12.wireOp",EDGE,"E78"),sQuery(id+"F12.wireOp",EDGE,"E79.MirrorCS"),sQuery(id+"F12.wireOp",EDGE,"E80"),sQuery(id+"F12.wireOp",EDGE,"E81"),sQuery(id+"F12.wireOp",EDGE,"E82")])],"isStart":false});
            var sketch = newSketch(context, id + "F16", { "sketchPlane" : qUnion([Q0])});
            skPoint(sketch, "E97.0", {"position": v(-55.65, 144) * mm});
            skPoint(sketch, "E98.0", {"position": v(-110.64, 175.75) * mm});
            skPoint(sketch, "E99.0", {"position": v(-125.1, 23.7) * mm});
            skPoint(sketch, "E100.0", {"position": v(-180.1, 55.45) * mm});
            skPoint(sketch, "E101.0", {"position": v(-57.94, 203.53) * mm});
            skPoint(sketch, "E102.0", {"position": v(-109.14, 203.75) * mm});
            skSolve(sketch);
        }
        {
            var Q0;
            Q0=sQuery(id+"F16.wireOp",VERTEX,"E97.0");
            var Q1;
            Q1=sQuery(id+"F16.wireOp",VERTEX,"E98.0");
            var Q2;
            Q2=sQuery(id+"F16.wireOp",VERTEX,"E99.0");
            var Q3;
            Q3=sQuery(id+"F16.wireOp",VERTEX,"E100.0");
            var Q4;
            Q4=makeQuery(id+"F14.opExtrude","SWEPT_BODY",BODY,{"disambiguationData":[OSD([sQuery(id+"F12.wireOp",EDGE,"E68"),sQuery(id+"F12.wireOp",EDGE,"E69"),sQuery(id+"F12.wireOp",EDGE,"E70"),sQuery(id+"F12.wireOp",EDGE,"E71"),sQuery(id+"F12.wireOp",EDGE,"E77"),sQuery(id+"F12.wireOp",EDGE,"E78"),sQuery(id+"F12.wireOp",EDGE,"E79.MirrorCS"),sQuery(id+"F12.wireOp",EDGE,"E80"),sQuery(id+"F12.wireOp",EDGE,"E81"),sQuery(id+"F12.wireOp",EDGE,"E82")])]});
            hole(context, id + "F17", {"style" : HoleStyle.C_BORE, "endStyle" : HoleEndStyle.THROUGH, "holeDiameter" : 16 * mm, "cBoreDiameter" : 32.5 * mm, "cBoreDepth" : 16 * mm, "majorDiameter" : 6.35 * mm, "isTappedThrough" : true, "tappedDepth" : 12.7 * mm, "tapClearance" : 3, "startFromSketch" : true, "locations" : qUnion([Q0, Q1, Q2, Q3]), "scope" : qUnion([Q4])});
        }
        {
            var Q0;
            Q0=sQuery(id+"F12.wireOp",VERTEX,"E74");
            var Q1;
            Q1=sQuery(id+"F12.wireOp",VERTEX,"E73");
            var Q2;
            Q2=sQuery(id+"F12.wireOp",VERTEX,"E75");
            var Q3;
            Q3=makeQuery(id+"F14.opExtrude","SWEPT_BODY",BODY,{"disambiguationData":[OSD([sQuery(id+"F12.wireOp",EDGE,"E68"),sQuery(id+"F12.wireOp",EDGE,"E69"),sQuery(id+"F12.wireOp",EDGE,"E70"),sQuery(id+"F12.wireOp",EDGE,"E71"),sQuery(id+"F12.wireOp",EDGE,"E77"),sQuery(id+"F12.wireOp",EDGE,"E78"),sQuery(id+"F12.wireOp",EDGE,"E79.MirrorCS")])]});
            hole(context, id + "F18", {"style" : HoleStyle.SIMPLE, "endStyle" : HoleEndStyle.THROUGH, "oppositeDirection" : true, "standardTappedOrClearance" : lookupTablePath({ "standard" : "ISO", "engagement" : "75%", "pitch" : "1.25 mm", "size" : "M8", "type" : "Tapped" }), "standardBlindInLast" : lookupTablePath({ "standard" : "ISO", "fit" : "Normal", "engagement" : "75%", "pitch" : "1.25 mm", "size" : "M8", "type" : "Clearance & tapped" }), "holeDiameter" : 6.8 * mm, "majorDiameter" : 8 * mm, "showTappedDepth" : true, "isTappedThrough" : true, "tappedDepth" : 12.7 * mm, "tapClearance" : 3, "startFromSketch" : true, "locations" : qUnion([Q0, Q1, Q2]), "scope" : qUnion([Q3])});
        }
        {
            var Q0;
            Q0=sQuery(id+"F12.wireOp",VERTEX,"E85.end");
            var Q1;
            Q1=sQuery(id+"F12.wireOp",VERTEX,"E86.end");
            var Q2;
            Q2=sQuery(id+"F12.wireOp",VERTEX,"E91.end");
            var Q3;
            Q3=sQuery(id+"F12.wireOp",VERTEX,"E92.end");
            var Q4;
            Q4=makeQuery(id+"F8.opExtrude","SWEPT_BODY",BODY,{"disambiguationData":[OSD([sQuery(id+"F7.wireOp",EDGE,"E39"),sQuery(id+"F7.wireOp",EDGE,"E40"),sQuery(id+"F7.wireOp",EDGE,"E41"),sQuery(id+"F7.wireOp",EDGE,"E42"),sQuery(id+"F7.wireOp",EDGE,"E43"),sQuery(id+"F7.wireOp",EDGE,"E55"),sQuery(id+"F7.wireOp",EDGE,"E56.filletArc"),sQuery(id+"F7.wireOp",EDGE,"E57.filletArc"),sQuery(id+"F7.wireOp",EDGE,"E58.filletArc")])]});
            hole(context, id + "F19", {"style" : HoleStyle.SIMPLE, "endStyle" : HoleEndStyle.THROUGH, "standardTappedOrClearance" : lookupTablePath({ "standard" : "ISO", "engagement" : "75%", "pitch" : "2 mm", "size" : "M16", "type" : "Tapped" }), "standardBlindInLast" : lookupTablePath({ "standard" : "ISO", "fit" : "Normal", "engagement" : "75%", "pitch" : "2 mm", "size" : "M16", "type" : "Clearance & tapped" }), "holeDiameter" : 14 * mm, "majorDiameter" : 16 * mm, "showTappedDepth" : true, "isTappedThrough" : true, "tappedDepth" : 12.7 * mm, "tapClearance" : 3, "startFromSketch" : true, "locations" : qUnion([Q0, Q1, Q2, Q3]), "scope" : qUnion([Q4])});
        }
        {
            var Q0;
            Q0=makeQuery(id+"F8.opExtrude","CAP_FACE",FACE,{"disambiguationData":[OSD([sQuery(id+"F7.wireOp",EDGE,"E39"),sQuery(id+"F7.wireOp",EDGE,"E40"),sQuery(id+"F7.wireOp",EDGE,"E41"),sQuery(id+"F7.wireOp",EDGE,"E42"),sQuery(id+"F7.wireOp",EDGE,"E43"),sQuery(id+"F7.wireOp",EDGE,"E55"),sQuery(id+"F7.wireOp",EDGE,"E56.filletArc"),sQuery(id+"F7.wireOp",EDGE,"E57.filletArc"),sQuery(id+"F7.wireOp",EDGE,"E58.filletArc")])],"isStart":false});
            var sketch = newSketch(context, id + "F20", { "sketchPlane" : qUnion([Q0])});
            skArc(sketch, "E103.0.0", {"start": v(-253.09, 68.73) * mm, "mid": v(-229.92, -26.23) * mm, "end": v(-165.1, -99.4) * mm});
            skLineSegment(sketch, "E103.0.1", {"start": v(-165.1, -99.4) * mm, "end": v(-138.91, -114.51) * mm});
            skArc(sketch, "E103.0.2", {"start": v(-138.91, -114.51) * mm, "mid": v(-129.27, -115.78) * mm, "end": v(-121.56, -109.86) * mm});
            skLineSegment(sketch, "E103.0.3", {"start": v(-121.56, -109.86) * mm, "end": v(30.84, 154.1) * mm});
            skArc(sketch, "E103.0.4", {"start": v(30.84, 154.1) * mm, "mid": v(32.1, 163.74) * mm, "end": v(26.19, 171.45) * mm});
            skLineSegment(sketch, "E103.0.5", {"start": v(26.19, 171.45) * mm, "end": v(-47.85, 214.2) * mm});
            skArc(sketch, "E103.0.6", {"start": v(-127.79, 260.35) * mm, "mid": v(-137.43, 261.62) * mm, "end": v(-145.14, 255.7) * mm});
            skLineSegment(sketch, "E103.0.7", {"start": v(-171.78, 209.55) * mm, "end": v(-253.09, 68.73) * mm});
            skLineSegment(sketch, "E104.0", {"start": v(-165.1, -212.73) * mm, "end": v(-165.1, -66) * mm});
            skArc(sketch, "E105.0", {"start": v(-165.1, 66) * mm, "mid": v(-177.8, 0) * mm, "end": v(-165.1, -66) * mm});
            skCircle(sketch, "E106.0", {"center": v(-180.1, 55.45) * mm, "radius": 20 * mm});
            skLineSegment(sketch, "E107.0", {"start": v(-165.1, 188.91) * mm, "end": v(-165.1, 66) * mm});
            skLineSegment(sketch, "E108.0", {"start": v(-165.1, 215.9) * mm, "end": v(-165.1, 200.02) * mm});
            skLineSegment(sketch, "E109.0", {"start": v(-165.1, 215.9) * mm, "end": v(-54.2, 215.9) * mm});
            skLineSegment(sketch, "E110.0", {"start": v(-165.1, 188.91) * mm, "end": v(-165.1, 200.02) * mm});
            skLineSegment(sketch, "E111", {"start": v(-165.1, 215.9) * mm, "end": v(-165.1, 221.13) * mm});
            skArc(sketch, "E112", {"start": v(-165.1, 221.13) * mm, "mid": v(-222.04, 60.87) * mm, "end": v(-165.1, -99.4) * mm});
            skPoint(sketch, "E113", {"position": v(-50.8, 215.9) * mm});
            skLineSegment(sketch, "E114", {"start": v(-160.79, 215.9) * mm, "end": v(-165.1, 215.9) * mm});
            skPoint(sketch, "E115.newPointA", {"position": v(-127.79, 260.35) * mm});
            skPoint(sketch, "E115.newPointB", {"position": v(165.1, 215.9) * mm});
            skArc(sketch, "E115.filletArc", {"start": v(-47.85, 214.2) * mm, "mid": v(-50.92, 215.47) * mm, "end": v(-54.2, 215.9) * mm});
            skArc(sketch, "E116.filletArc", {"start": v(-160.79, 215.9) * mm, "mid": v(-167.14, 214.2) * mm, "end": v(-171.78, 209.55) * mm});
            skSolve(sketch);
        }
        {
            var Q0;
            {var subQ0=sQuery(id+"F20.wireOp",EDGE,"E103.0.0");Q0=makeQuery(id+"F20.imprint","IMPRINT",FACE,{"disambiguationData":[TD([[makeQuery(id+"F20.imprint","IMPRINT",EDGE,{"derivedFrom":subQ0}),1.0]])]});}
            var Q1;
            {var subQ1=sQuery(id+"F20.wireOp",EDGE,"E103.0.6");Q1=makeQuery(id+"F20.imprint","IMPRINT",FACE,{"disambiguationData":[TD([[makeQuery(id+"F20.imprint","IMPRINT",EDGE,{"derivedFrom":subQ1}),1.0]])]});}
            var Q2;
            {var subQ0=sQuery(id+"F20.wireOp",EDGE,"E111");Q2=makeQuery(id+"F20.imprint","IMPRINT",FACE,{"disambiguationData":[TD([[makeQuery(id+"F20.imprint","IMPRINT",EDGE,{"derivedFrom":subQ0}),1.0]])]});}
            var Q3;
            {var subQ0=sQuery(id+"F20.wireOp",EDGE,"E114");Q3=makeQuery(id+"F20.imprint","IMPRINT",FACE,{"disambiguationData":[TD([[makeQuery(id+"F20.imprint","IMPRINT",EDGE,{"derivedFrom":subQ0}),1.0]])]});}
            var Q4;
            Q4=makeQuery(id+"F8.opExtrude","CAP_FACE",FACE,{"disambiguationData":[OSD([sQuery(id+"F7.wireOp",EDGE,"E39"),sQuery(id+"F7.wireOp",EDGE,"E40"),sQuery(id+"F7.wireOp",EDGE,"E41"),sQuery(id+"F7.wireOp",EDGE,"E42"),sQuery(id+"F7.wireOp",EDGE,"E43"),sQuery(id+"F7.wireOp",EDGE,"E55"),sQuery(id+"F7.wireOp",EDGE,"E56.filletArc"),sQuery(id+"F7.wireOp",EDGE,"E57.filletArc"),sQuery(id+"F7.wireOp",EDGE,"E58.filletArc")])],"isStart":true});
            extrude(context, id + "F21", {"entities" : qUnion([Q0, Q1, Q2, Q3]), "operationType" : NewBodyOperationType.REMOVE, "endBound" : BoundingType.UP_TO_SURFACE, "oppositeDirection" : true, "depth" : 25.4 * mm, "endBoundEntityFace" : qUnion([Q4]), "offsetDistance" : 25.4 * mm});
        }
    });
